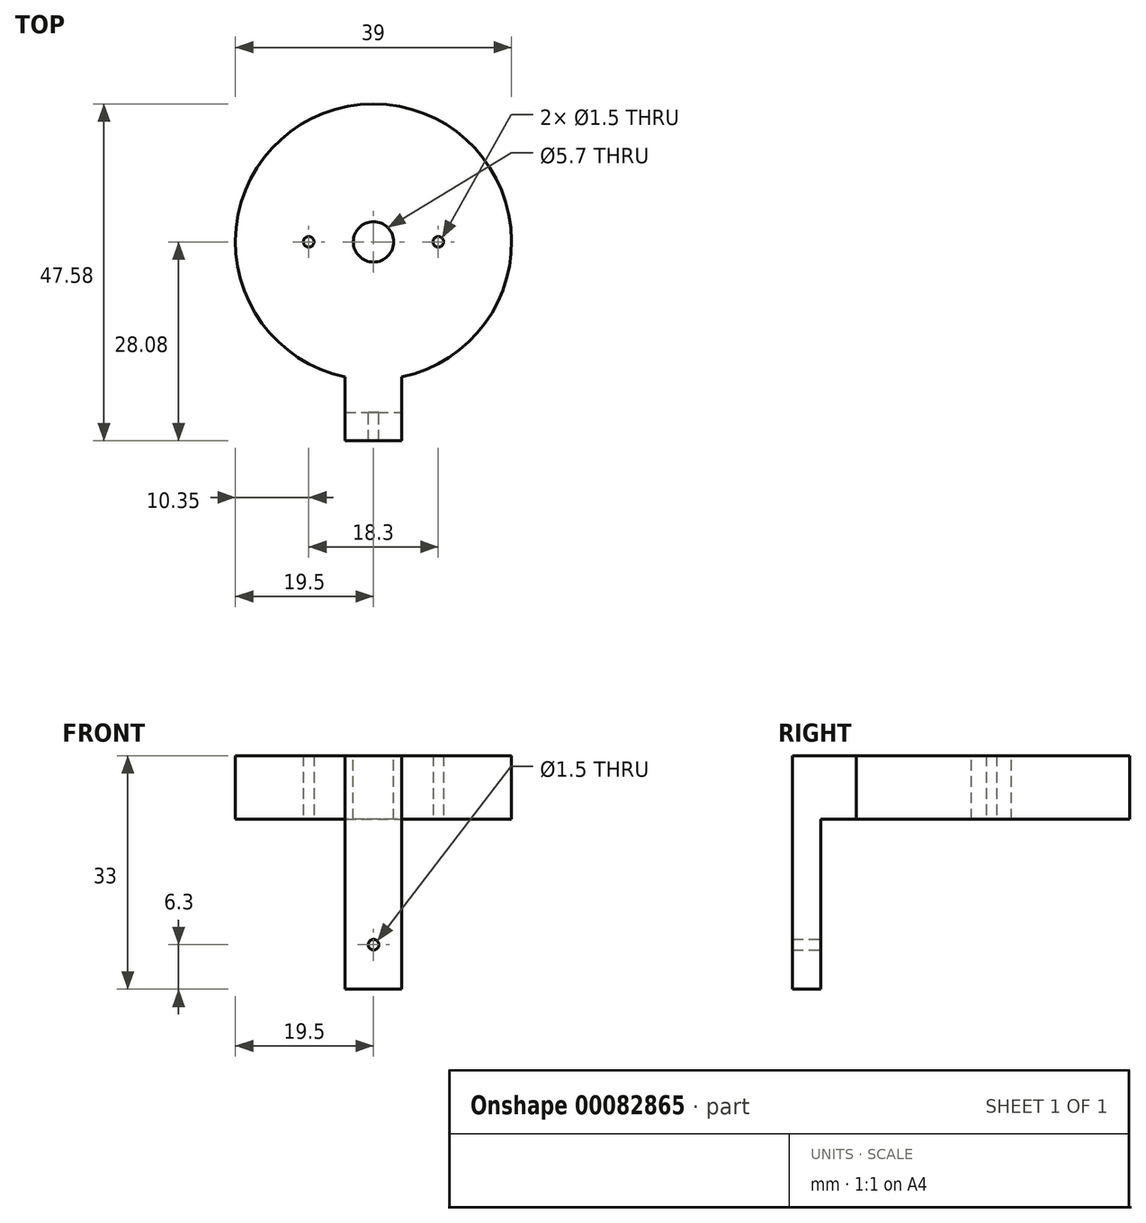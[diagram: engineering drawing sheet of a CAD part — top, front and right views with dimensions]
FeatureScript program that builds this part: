
annotation { "Feature Type Name" : "Feature", "Feature Type Description" : "" }
export const myFeature = defineFeature(function(context is Context, id is Id, definition is map)
    precondition{}
    {
        {
            var Q0;
            Q0=qCreatedBy(makeId("Top.planeOp"),FACE);
            var sketch = newSketch(context, id + "F0", { "sketchPlane" : qUnion([Q0])});
            skCircle(sketch, "E0", {"center": v(0, 0) * mm, "radius": 19.5 * mm});
            skSolve(sketch);
        }
        {
            var Q0;
            Q0=qSketchRegion(id+"F0",true);
            extrude(context, id + "F1", {"entities" : qUnion([Q0]), "depth" : 9 * mm});
        }
        {
            var Q0;
            Q0=makeQuery(id+"F1.opExtrude","CAP_FACE",FACE,{"disambiguationData":[OSD([sQuery(id+"F0.wireOp",EDGE,"E0")])],"isStart":false});
            var sketch = newSketch(context, id + "F2", { "sketchPlane" : qUnion([Q0])});
            skCircle(sketch, "E1", {"center": v(0, 0) * mm, "radius": 2.85 * mm});
            skSolve(sketch);
        }
        {
            var Q0;
            Q0=qSketchRegion(id+"F2",true);
            extrude(context, id + "F3", {"entities" : qUnion([Q0]), "operationType" : NewBodyOperationType.REMOVE, "endBound" : BoundingType.THROUGH_ALL, "oppositeDirection" : true, "depth" : 25 * mm});
        }
        {
            var Q0;
            Q0=makeQuery(id+"F1.opExtrude","CAP_FACE",FACE,{"disambiguationData":[OSD([sQuery(id+"F0.wireOp",EDGE,"E0")])],"isStart":true});
            var sketch = newSketch(context, id + "F4", { "sketchPlane" : qUnion([Q0])});
            skLineSegment(sketch, "E2.bottom", {"start": v(-4, 28.08) * mm, "end": v(4, 28.08) * mm});
            skLineSegment(sketch, "E2.top", {"start": v(-4, 19.08) * mm, "end": v(4, 19.08) * mm});
            skLineSegment(sketch, "E2.left", {"start": v(-4, 28.08) * mm, "end": v(-4, 19.08) * mm});
            skLineSegment(sketch, "E2.right", {"start": v(4, 28.08) * mm, "end": v(4, 19.08) * mm});
            skSolve(sketch);
        }
        {
            var Q0;
            Q0=qSketchRegion(id+"F4",true);
            extrude(context, id + "F5", {"entities" : qUnion([Q0]), "operationType" : NewBodyOperationType.ADD, "oppositeDirection" : true, "depth" : 9 * mm});
        }
        {
            var Q0;
            Q0=makeQuery(id+"F5.boolean.opBoolean","MERGE",FACE,{"derivedFrom":[makeQuery(id+"F1.opExtrude","CAP_FACE",FACE,{"disambiguationData":[OSD([sQuery(id+"F0.wireOp",EDGE,"E0")])],"isStart":true}),makeQuery(id+"F5.opExtrude","CAP_FACE",FACE,{"disambiguationData":[OSD([sQuery(id+"F4.wireOp",EDGE,"E2.bottom"),sQuery(id+"F4.wireOp",EDGE,"E2.top"),sQuery(id+"F4.wireOp",EDGE,"E2.left"),sQuery(id+"F4.wireOp",EDGE,"E2.right")])],"isStart":true})]});
            var sketch = newSketch(context, id + "F6", { "sketchPlane" : qUnion([Q0])});
            skLineSegment(sketch, "E3.bottom", {"start": v(-4, 28.08) * mm, "end": v(4, 28.08) * mm});
            skLineSegment(sketch, "E3.top", {"start": v(-4, 24.08) * mm, "end": v(4, 24.08) * mm});
            skLineSegment(sketch, "E3.left", {"start": v(-4, 28.08) * mm, "end": v(-4, 24.08) * mm});
            skLineSegment(sketch, "E3.right", {"start": v(4, 28.08) * mm, "end": v(4, 24.08) * mm});
            skSolve(sketch);
        }
        {
            var Q0;
            Q0=qSketchRegion(id+"F6",true);
            extrude(context, id + "F7", {"entities" : qUnion([Q0]), "operationType" : NewBodyOperationType.ADD, "depth" : 24 * mm});
        }
        {
            var Q0;
            Q0=makeQuery(id+"F5.boolean.opBoolean","MERGE",FACE,{"derivedFrom":[makeQuery(id+"F1.opExtrude","CAP_FACE",FACE,{"disambiguationData":[OSD([sQuery(id+"F0.wireOp",EDGE,"E0")])],"isStart":true}),makeQuery(id+"F5.opExtrude","CAP_FACE",FACE,{"disambiguationData":[OSD([sQuery(id+"F4.wireOp",EDGE,"E2.bottom"),sQuery(id+"F4.wireOp",EDGE,"E2.top"),sQuery(id+"F4.wireOp",EDGE,"E2.left"),sQuery(id+"F4.wireOp",EDGE,"E2.right")])],"isStart":true})]});
            var sketch = newSketch(context, id + "F8", { "sketchPlane" : qUnion([Q0])});
            skCircle(sketch, "E4", {"center": v(-9.15, 0) * mm, "radius": 0.75 * mm});
            skLineSegment(sketch, "E5", {"start": v(2.85, 0) * mm, "end": v(9.15, 0) * mm, "construction": true});
            skLineSegment(sketch, "E6", {"start": v(-2.85, 0) * mm, "end": v(-9.15, 0) * mm, "construction": true});
            skCircle(sketch, "E7", {"center": v(9.15, 0) * mm, "radius": 0.75 * mm});
            skSolve(sketch);
        }
        {
            var Q0;
            Q0=qSketchRegion(id+"F8",true);
            extrude(context, id + "F9", {"entities" : qUnion([Q0]), "operationType" : NewBodyOperationType.REMOVE, "endBound" : BoundingType.THROUGH_ALL, "oppositeDirection" : true, "depth" : 25 * mm});
        }
        {
            var Q0;
            Q0=makeQuery(id+"F7.opExtrude","SWEPT_FACE",FACE,{"disambiguationData":[OSD([sQuery(id+"F6.wireOp",EDGE,"E3.top")])]});
            var sketch = newSketch(context, id + "F10", { "sketchPlane" : qUnion([Q0])});
            skLineSegment(sketch, "E8", {"start": v(0, -24) * mm, "end": v(0, -17.7) * mm, "construction": true});
            skPoint(sketch, "E8.endSnap0", {"position": v(0, -24) * mm});
            skCircle(sketch, "E9", {"center": v(0, -17.7) * mm, "radius": 0.75 * mm});
            skSolve(sketch);
        }
        {
            var Q0;
            Q0=qSketchRegion(id+"F10",true);
            extrude(context, id + "F11", {"entities" : qUnion([Q0]), "operationType" : NewBodyOperationType.REMOVE, "endBound" : BoundingType.THROUGH_ALL, "oppositeDirection" : true, "depth" : 25 * mm});
        }
    });
